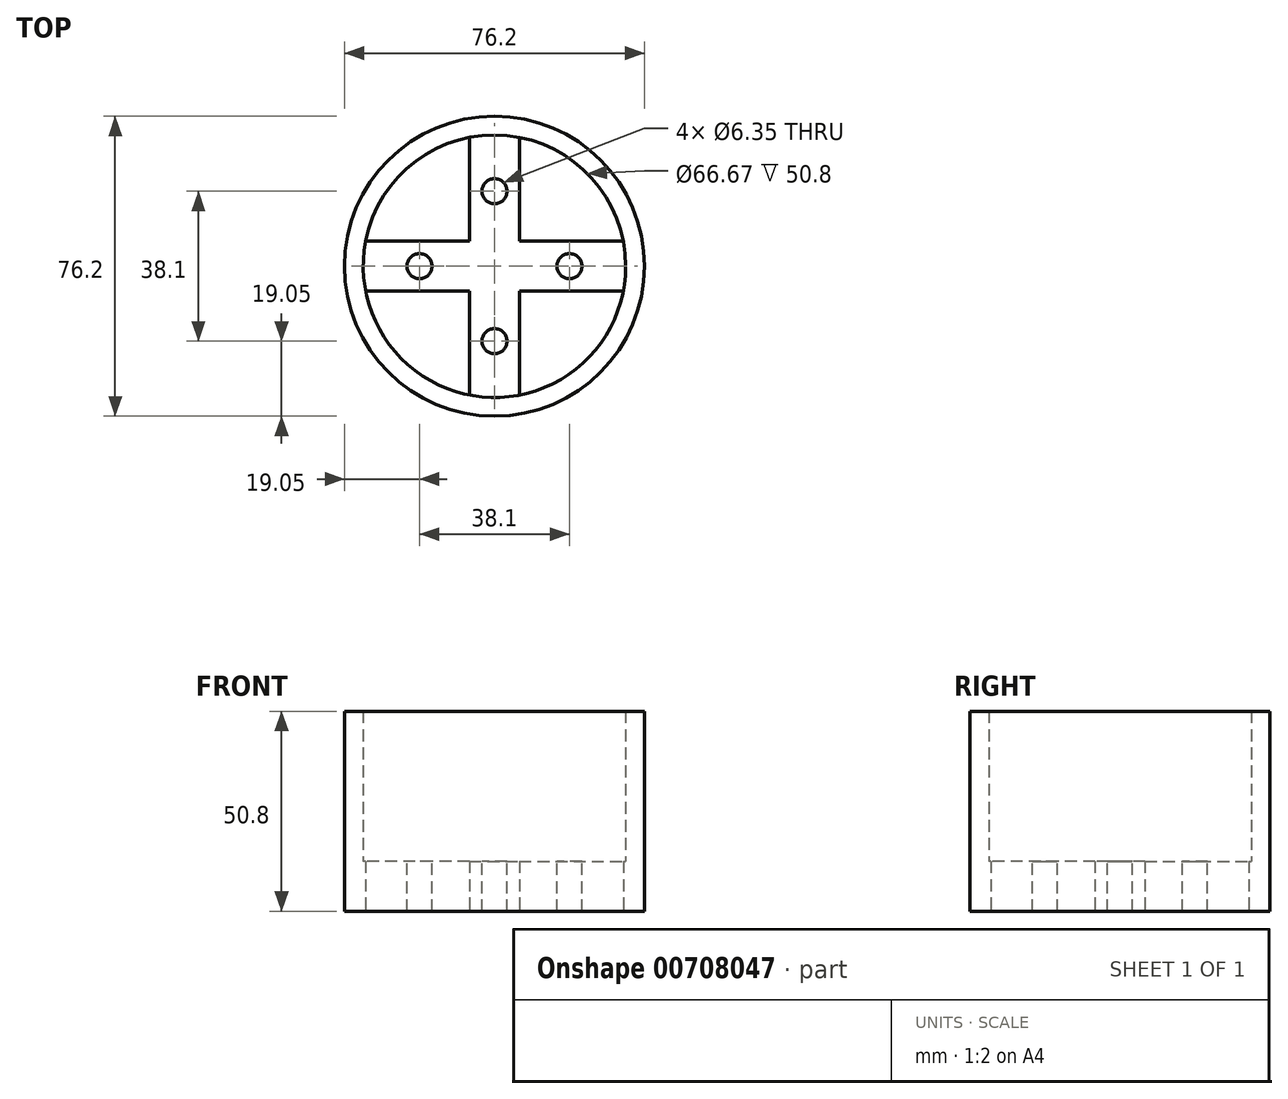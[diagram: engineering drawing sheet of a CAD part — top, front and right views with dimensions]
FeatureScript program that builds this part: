
annotation { "Feature Type Name" : "Feature", "Feature Type Description" : "" }
export const myFeature = defineFeature(function(context is Context, id is Id, definition is map)
    precondition{}
    {
        {
            var Q0;
            Q0=qCreatedBy(makeId("Top.planeOp"),FACE);
            var sketch = newSketch(context, id + "F0", { "sketchPlane" : qUnion([Q0])});
            skCircle(sketch, "E0", {"center": v(0, 0) * mm, "radius": 38.1 * mm});
            skCircle(sketch, "E1", {"center": v(0, 0) * mm, "radius": 33.34 * mm});
            skSolve(sketch);
        }
        {
            var Q0;
            Q0=makeQuery(id+"F0.imprint","IMPRINT",FACE,{"disambiguationData":[TD([[makeQuery(id+"F0.imprint","IMPRINT",EDGE,{"derivedFrom":sQuery(id+"F0.wireOp",EDGE,"E0")}),1.0]])]});
            extrude(context, id + "F1", {"entities" : qUnion([Q0]), "depth" : 50.8 * mm, "offsetDistance" : 25.4 * mm});
        }
        {
            var Q0;
            Q0=qCreatedBy(makeId("Top.planeOp"),FACE);
            var sketch = newSketch(context, id + "F2", { "sketchPlane" : qUnion([Q0])});
            skLineSegment(sketch, "E2.left", {"start": v(-6.35, 6.35) * mm, "end": v(-6.35, 35.35) * mm});
            skLineSegment(sketch, "E2.right", {"start": v(6.35, 6.35) * mm, "end": v(6.35, 35.35) * mm});
            skLineSegment(sketch, "E3.left", {"start": v(-6.35, -6.35) * mm, "end": v(-6.35, -35.28) * mm});
            skLineSegment(sketch, "E3.right", {"start": v(6.35, -6.35) * mm, "end": v(6.35, -35.28) * mm});
            skLineSegment(sketch, "E4.bottom", {"start": v(-6.35, 6.35) * mm, "end": v(-35.76, 6.35) * mm});
            skLineSegment(sketch, "E4.top", {"start": v(-6.35, -6.35) * mm, "end": v(-35.76, -6.35) * mm});
            skLineSegment(sketch, "E5.bottom", {"start": v(6.35, 6.35) * mm, "end": v(35.55, 6.35) * mm});
            skLineSegment(sketch, "E5.top", {"start": v(6.35, -6.35) * mm, "end": v(35.55, -6.35) * mm});
            skPoint(sketch, "E6.start.orphan", {"position": v(-6.35, 0) * mm});
            skPoint(sketch, "E7.start.orphan", {"position": v(6.35, 0) * mm});
            skLineSegment(sketch, "E8", {"start": v(-35.76, 6.35) * mm, "end": v(-35.76, -6.35) * mm});
            skLineSegment(sketch, "E9", {"start": v(-6.35, -35.28) * mm, "end": v(6.35, -35.28) * mm});
            skLineSegment(sketch, "E10", {"start": v(35.55, -6.35) * mm, "end": v(35.55, 6.35) * mm});
            skLineSegment(sketch, "E11", {"start": v(-6.35, 35.35) * mm, "end": v(6.35, 35.35) * mm});
            skSolve(sketch);
        }
        {
            var Q0;
            Q0=makeQuery(id+"F2.imprint","IMPRINT",FACE,{"disambiguationData":[TD([[makeQuery(id+"F2.imprint","IMPRINT",EDGE,{"derivedFrom":sQuery(id+"F2.wireOp",EDGE,"E2.left")}),-1.0]])]});
            extrude(context, id + "F3", {"entities" : qUnion([Q0]), "operationType" : NewBodyOperationType.ADD, "depth" : 12.7 * mm, "offsetDistance" : 25.4 * mm});
        }
        {
            var Q0;
            Q0=makeQuery(id+"F3.opExtrude","CAP_FACE",FACE,{"disambiguationData":[OSD([sQuery(id+"F2.wireOp",EDGE,"E2.left"),sQuery(id+"F2.wireOp",EDGE,"E2.right"),sQuery(id+"F2.wireOp",EDGE,"E3.left"),sQuery(id+"F2.wireOp",EDGE,"E3.right"),sQuery(id+"F2.wireOp",EDGE,"E4.bottom"),sQuery(id+"F2.wireOp",EDGE,"E4.top"),sQuery(id+"F2.wireOp",EDGE,"E5.bottom"),sQuery(id+"F2.wireOp",EDGE,"E5.top"),sQuery(id+"F2.wireOp",EDGE,"E8"),sQuery(id+"F2.wireOp",EDGE,"E9"),sQuery(id+"F2.wireOp",EDGE,"E10"),sQuery(id+"F2.wireOp",EDGE,"E11")])],"isStart":false});
            var sketch = newSketch(context, id + "F4", { "sketchPlane" : qUnion([Q0])});
            skLineSegment(sketch, "E12", {"start": v(0, 0) * mm, "end": v(0, 19.05) * mm, "construction": true});
            skLineSegment(sketch, "E13", {"start": v(0, 0) * mm, "end": v(0, -19.05) * mm, "construction": true});
            skLineSegment(sketch, "E14", {"start": v(0, 0) * mm, "end": v(19.05, 0) * mm, "construction": true});
            skLineSegment(sketch, "E15", {"start": v(0, 0) * mm, "end": v(-19.05, 0) * mm, "construction": true});
            skCircle(sketch, "E16", {"center": v(-19.05, 0) * mm, "radius": 3.18 * mm});
            skCircle(sketch, "E17", {"center": v(0, 19.05) * mm, "radius": 3.18 * mm});
            skCircle(sketch, "E18", {"center": v(19.05, 0) * mm, "radius": 3.18 * mm});
            skCircle(sketch, "E19", {"center": v(0, -19.05) * mm, "radius": 3.18 * mm});
            skSolve(sketch);
        }
        {
            var Q0;
            Q0=makeQuery(id+"F4.imprint","IMPRINT",FACE,{"disambiguationData":[TD([[makeQuery(id+"F4.imprint","IMPRINT",EDGE,{"derivedFrom":sQuery(id+"F4.wireOp",EDGE,"E16")}),1.0]])]});
            var Q1;
            Q1=makeQuery(id+"F4.imprint","IMPRINT",FACE,{"disambiguationData":[TD([[makeQuery(id+"F4.imprint","IMPRINT",EDGE,{"derivedFrom":sQuery(id+"F4.wireOp",EDGE,"E18")}),1.0]])]});
            var Q2;
            Q2=makeQuery(id+"F4.imprint","IMPRINT",FACE,{"disambiguationData":[TD([[makeQuery(id+"F4.imprint","IMPRINT",EDGE,{"derivedFrom":sQuery(id+"F4.wireOp",EDGE,"E17")}),1.0]])]});
            var Q3;
            Q3=makeQuery(id+"F4.imprint","IMPRINT",FACE,{"disambiguationData":[TD([[makeQuery(id+"F4.imprint","IMPRINT",EDGE,{"derivedFrom":sQuery(id+"F4.wireOp",EDGE,"E19")}),1.0]])]});
            extrude(context, id + "F5", {"entities" : qUnion([Q0, Q1, Q2, Q3]), "operationType" : NewBodyOperationType.REMOVE, "oppositeDirection" : true, "depth" : 25.4 * mm, "offsetDistance" : 25.4 * mm});
        }
    });
